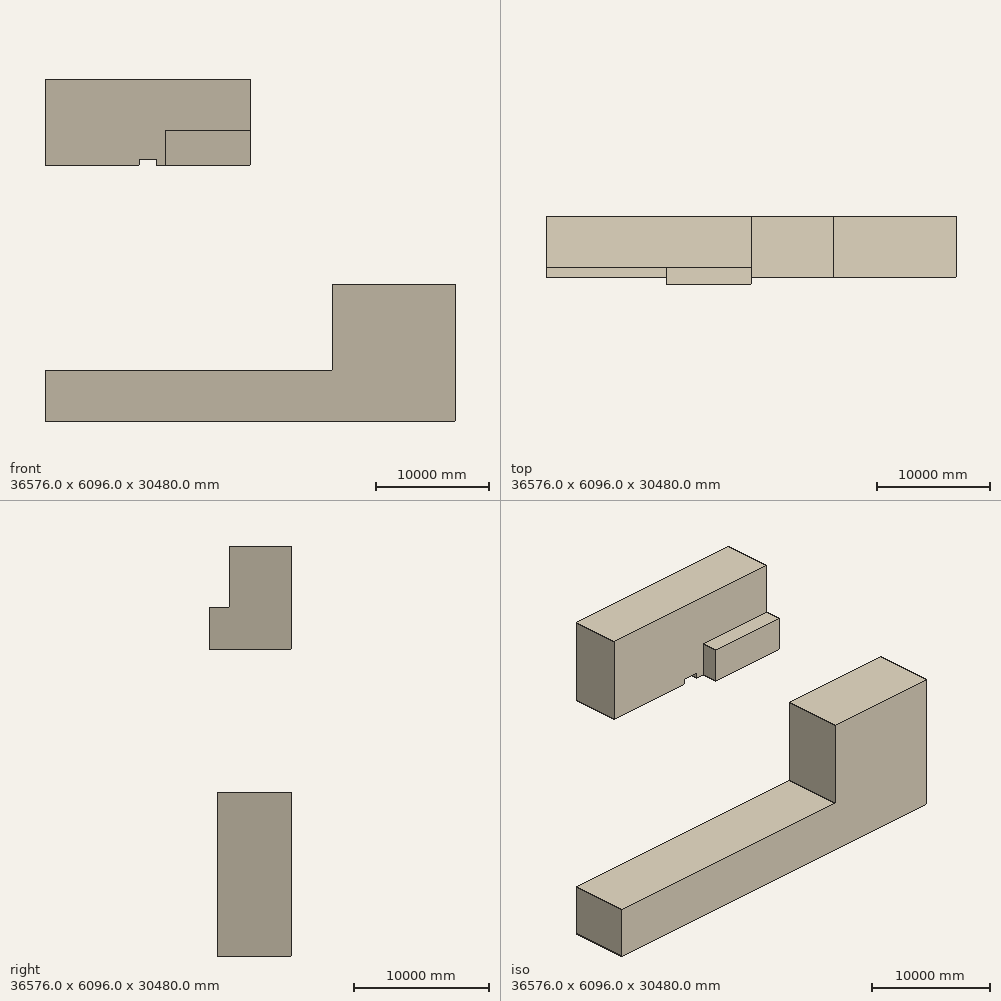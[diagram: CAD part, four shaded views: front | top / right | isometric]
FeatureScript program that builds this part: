
annotation { "Feature Type Name" : "Feature", "Feature Type Description" : "" }
export const myFeature = defineFeature(function(context is Context, id is Id, definition is map)
    precondition{}
    {
        {
            var Q0;
            Q0=qCreatedBy(makeId("Front.planeOp"),FACE);
            var sketch = newSketch(context, id + "F0", { "sketchPlane" : qUnion([Q0])});
            skLineSegment(sketch, "E0", {"start": v(0, 0) * mm, "end": v(-36576, 0) * mm});
            skLineSegment(sketch, "E1", {"start": v(-36576, 0) * mm, "end": v(-36576, 30480) * mm});
            skLineSegment(sketch, "E2", {"start": v(-36576, 30480) * mm, "end": v(-18288, 30480) * mm});
            skLineSegment(sketch, "E3", {"start": v(-18288, 30480) * mm, "end": v(-18288, 20726.4) * mm});
            skLineSegment(sketch, "E4", {"start": v(0, 0) * mm, "end": v(0, 12192) * mm});
            skLineSegment(sketch, "E5", {"start": v(0, 12192) * mm, "end": v(-10972.8, 12192) * mm});
            skLineSegment(sketch, "E6", {"start": v(-18288, 20726.4) * mm, "end": v(-16018.93, 18079.15) * mm});
            skLineSegment(sketch, "E7", {"start": v(-13241.87, 14839.25) * mm, "end": v(-12894.74, 15136.8) * mm});
            skLineSegment(sketch, "E8", {"start": v(-12894.74, 15136.8) * mm, "end": v(-15671.8, 18376.7) * mm});
            skLineSegment(sketch, "E9", {"start": v(-15671.8, 18376.7) * mm, "end": v(-16018.93, 18079.15) * mm});
            skLineSegment(sketch, "E10.trimOffspring", {"start": v(-13241.87, 14839.25) * mm, "end": v(-10972.8, 12192) * mm});
            skLineSegment(sketch, "E11", {"start": v(-10972.8, 12192) * mm, "end": v(-10972.8, 4572) * mm});
            skLineSegment(sketch, "E12", {"start": v(-10972.8, 0) * mm, "end": v(-7924.8, 0) * mm});
            skLineSegment(sketch, "E13", {"start": v(-7924.8, 4572) * mm, "end": v(-7924.8, 12192) * mm});
            skLineSegment(sketch, "E14", {"start": v(-10972.8, 12192) * mm, "end": v(-10058.4, 12192) * mm});
            skLineSegment(sketch, "E15", {"start": v(-10058.4, 12192) * mm, "end": v(-10058.4, 4572) * mm});
            skPoint(sketch, "E16.orphan", {"position": v(-10058.4, 0) * mm});
            skLineSegment(sketch, "E17", {"start": v(-7924.8, 4572) * mm, "end": v(-36576, 4572) * mm});
            skLineSegment(sketch, "E18", {"start": v(-10972.8, 12192) * mm, "end": v(-7924.8, 12192) * mm});
            skLineSegment(sketch, "E19", {"start": v(-18288, 30480) * mm, "end": v(-18288, 22860) * mm});
            skLineSegment(sketch, "E20", {"start": v(-18288, 22860) * mm, "end": v(-26670, 22860) * mm});
            skLineSegment(sketch, "E21", {"start": v(-28194, 22860) * mm, "end": v(-28194, 23336.8) * mm});
            skLineSegment(sketch, "E22", {"start": v(-28194, 23336.8) * mm, "end": v(-26670, 23336.8) * mm});
            skLineSegment(sketch, "E23", {"start": v(-26670, 23336.8) * mm, "end": v(-26670, 22860) * mm});
            skLineSegment(sketch, "E24", {"start": v(-28194, 22860) * mm, "end": v(-28956, 22860) * mm});
            skLineSegment(sketch, "E25", {"start": v(-26670, 22860) * mm, "end": v(-25908, 22860) * mm});
            skLineSegment(sketch, "E26", {"start": v(-28956, 22860) * mm, "end": v(-28956, 25908) * mm});
            skLineSegment(sketch, "E27", {"start": v(-25908, 22860) * mm, "end": v(-25908, 25908) * mm});
            skLineSegment(sketch, "E28", {"start": v(-28956, 25908) * mm, "end": v(-36576, 25908) * mm});
            skLineSegment(sketch, "E29", {"start": v(-25908, 25908) * mm, "end": v(-18288, 25908) * mm});
            skPoint(sketch, "E30.start.orphan", {"position": v(-27432, 22860) * mm});
            skLineSegment(sketch, "E31.trimOffspring", {"start": v(-28194, 22860) * mm, "end": v(-36576, 22860) * mm});
            skSolve(sketch);
        }
        {
            var Q0;
            Q0=makeQuery(id+"F0.imprint","IMPRINT",FACE,{"disambiguationData":[TD([[makeQuery(id+"F0.imprint","IMPRINT",EDGE,{"derivedFrom":sQuery(id+"F0.wireOp",EDGE,"E3")}),-1.0]])]});
            extrude(context, id + "F1", {"entities" : qUnion([Q0]), "depth" : 6096 * mm, "offsetDistance" : 30.48 * mm});
        }
        {
            var Q0;
            {var subQ0=sQuery(id+"F0.wireOp",EDGE,"E20");Q0=makeQuery(id+"F0.imprint","IMPRINT",FACE,{"disambiguationData":[TD([[makeQuery(id+"F0.imprint","IMPRINT",EDGE,{"derivedFrom":subQ0}),-1.0]])]});}
            var Q1;
            {var subQ4=sQuery(id+"F0.wireOp",EDGE,"E26");Q1=makeQuery(id+"F0.imprint","IMPRINT",FACE,{"disambiguationData":[TD([[makeQuery(id+"F0.imprint","IMPRINT",EDGE,{"derivedFrom":subQ4}),1.0]])]});}
            var Q2;
            {var subQ2=sQuery(id+"F0.wireOp",EDGE,"E2");Q2=makeQuery(id+"F0.imprint","IMPRINT",FACE,{"disambiguationData":[TD([[makeQuery(id+"F0.imprint","IMPRINT",EDGE,{"derivedFrom":subQ2}),-1.0]])]});}
            extrude(context, id + "F2", {"entities" : qUnion([Q0, Q1, Q2]), "operationType" : NewBodyOperationType.ADD, "depth" : 4572 * mm, "offsetDistance" : 30.48 * mm});
        }
        {
            var Q0;
            {var subQ0=sQuery(id+"F0.wireOp",EDGE,"E11");Q0=makeQuery(id+"F0.imprint","IMPRINT",FACE,{"disambiguationData":[TD([[makeQuery(id+"F0.imprint","IMPRINT",EDGE,{"derivedFrom":subQ0}),1.0]])]});}
            var Q1;
            {var subQ0=sQuery(id+"F0.wireOp",EDGE,"E13");Q1=makeQuery(id+"F0.imprint","IMPRINT",FACE,{"disambiguationData":[TD([[makeQuery(id+"F0.imprint","IMPRINT",EDGE,{"derivedFrom":subQ0}),1.0]])]});}
            var Q2;
            {var subQ0=sQuery(id+"F0.wireOp",EDGE,"E4");Q2=makeQuery(id+"F0.imprint","IMPRINT",FACE,{"disambiguationData":[TD([[makeQuery(id+"F0.imprint","IMPRINT",EDGE,{"derivedFrom":subQ0}),1.0]])]});}
            extrude(context, id + "F3", {"entities" : qUnion([Q0, Q1, Q2]), "operationType" : NewBodyOperationType.ADD, "depth" : 5486.4 * mm, "offsetDistance" : 30.48 * mm});
        }
    });
